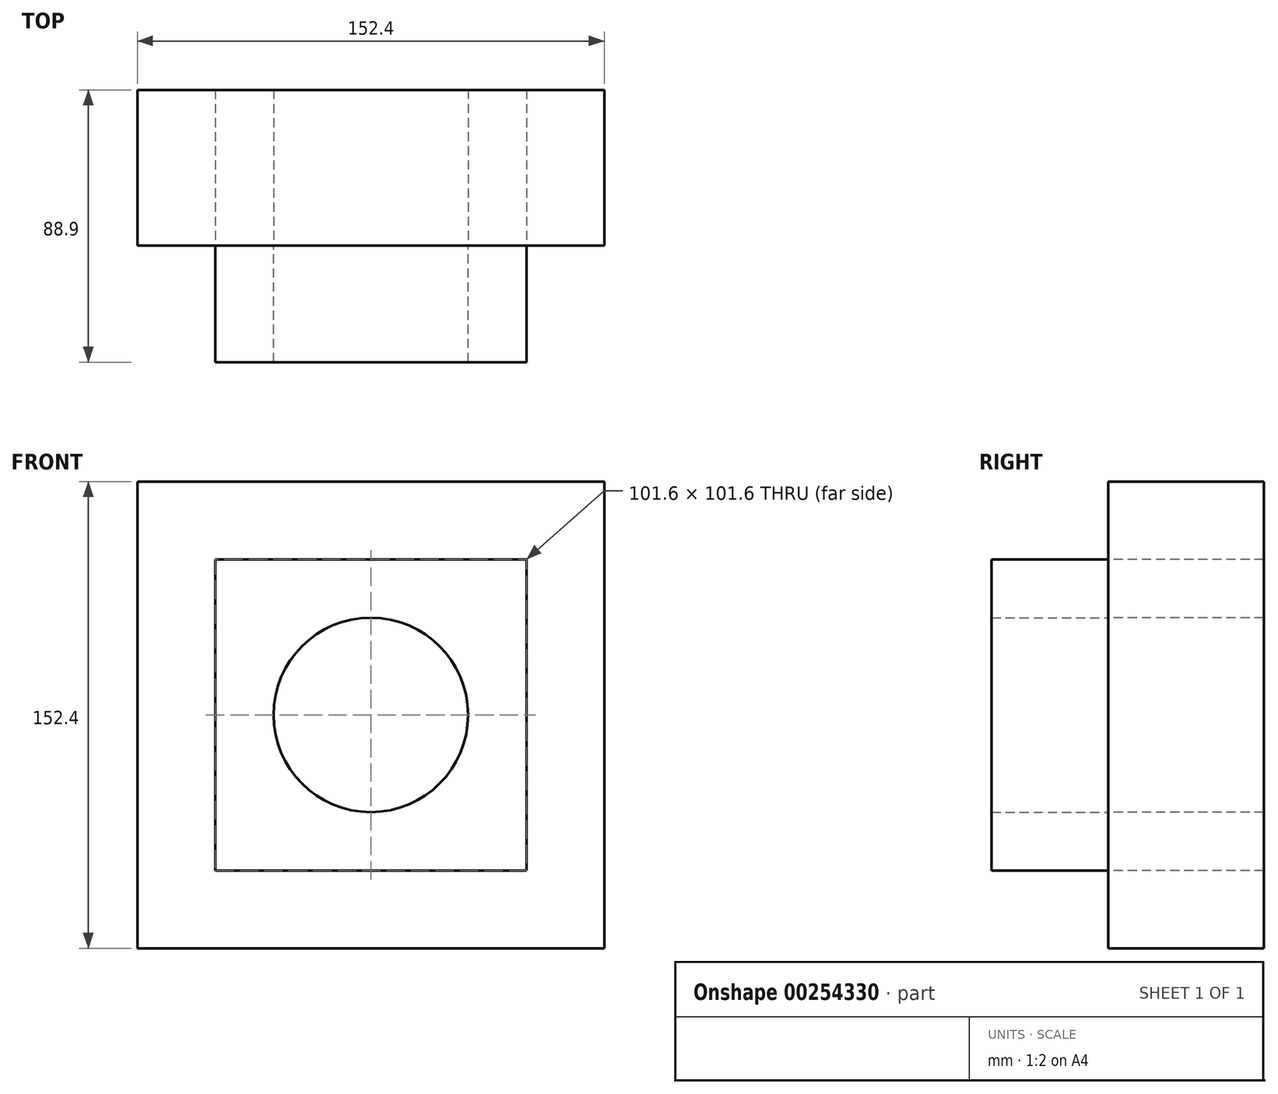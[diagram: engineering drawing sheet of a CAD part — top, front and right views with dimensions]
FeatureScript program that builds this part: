
annotation { "Feature Type Name" : "Feature", "Feature Type Description" : "" }
export const myFeature = defineFeature(function(context is Context, id is Id, definition is map)
    precondition{}
    {
        {
            var Q0;
            Q0=qCreatedBy(makeId("Front.planeOp"),FACE);
            var sketch = newSketch(context, id + "F0", { "sketchPlane" : qUnion([Q0])});
            skCircle(sketch, "E0", {"center": v(0, 0) * mm, "radius": 31.75 * mm});
            skLineSegment(sketch, "E1.bottom", {"start": v(50.8, 50.8) * mm, "end": v(-50.8, 50.8) * mm});
            skLineSegment(sketch, "E1.top", {"start": v(50.8, -50.8) * mm, "end": v(-50.8, -50.8) * mm});
            skLineSegment(sketch, "E1.left", {"start": v(50.8, 50.8) * mm, "end": v(50.8, -50.8) * mm});
            skLineSegment(sketch, "E1.right", {"start": v(-50.8, 50.8) * mm, "end": v(-50.8, -50.8) * mm});
            skLineSegment(sketch, "E2.bottom", {"start": v(76.2, 76.2) * mm, "end": v(-76.2, 76.2) * mm});
            skLineSegment(sketch, "E2.top", {"start": v(76.2, -76.2) * mm, "end": v(-76.2, -76.2) * mm});
            skLineSegment(sketch, "E2.left", {"start": v(76.2, 76.2) * mm, "end": v(76.2, -76.2) * mm});
            skLineSegment(sketch, "E2.right", {"start": v(-76.2, 76.2) * mm, "end": v(-76.2, -76.2) * mm});
            skSolve(sketch);
        }
        {
            var Q0;
            Q0=makeQuery(id+"F0.imprint","IMPRINT",FACE,{"disambiguationData":[TD([[makeQuery(id+"F0.imprint","IMPRINT",EDGE,{"derivedFrom":sQuery(id+"F0.wireOp",EDGE,"E0")}),-1.0]])]});
            extrude(context, id + "F1", {"entities" : qUnion([Q0]), "depth" : 38.1 * mm});
        }
        {
            var Q0;
            Q0=makeQuery(id+"F0.imprint","IMPRINT",FACE,{"disambiguationData":[TD([[makeQuery(id+"F0.imprint","IMPRINT",EDGE,{"derivedFrom":sQuery(id+"F0.wireOp",EDGE,"E1.bottom")}),-1.0]])]});
            extrude(context, id + "F2", {"entities" : qUnion([Q0]), "oppositeDirection" : true, "depth" : 50.8 * mm});
        }
        {
            var Q0;
            Q0=makeQuery(id+"F0.imprint","IMPRINT",FACE,{"disambiguationData":[TD([[makeQuery(id+"F0.imprint","IMPRINT",EDGE,{"derivedFrom":sQuery(id+"F0.wireOp",EDGE,"E0")}),1.0]])]});
            extrude(context, id + "F3", {"entities" : qUnion([Q0]), "operationType" : NewBodyOperationType.ADD, "oppositeDirection" : true, "depth" : 50.8 * mm});
        }
    });
